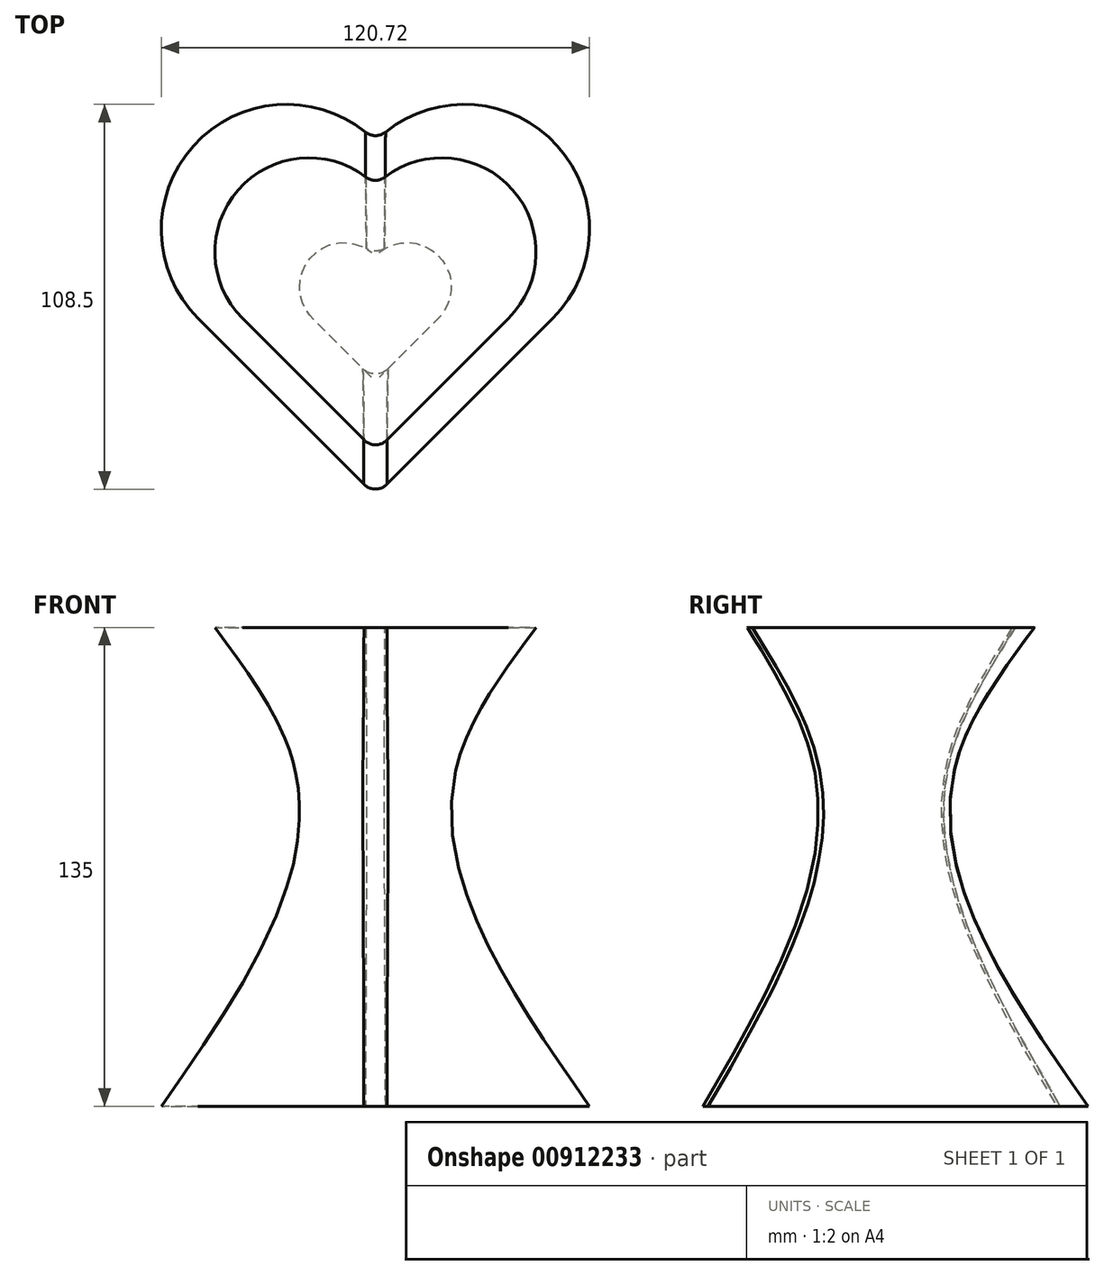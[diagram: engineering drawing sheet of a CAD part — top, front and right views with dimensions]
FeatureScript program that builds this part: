
annotation { "Feature Type Name" : "Feature", "Feature Type Description" : "" }
export const myFeature = defineFeature(function(context is Context, id is Id, definition is map)
    precondition{}
    {
        {
            var Q0;
            Q0=qCreatedBy(makeId("Top.planeOp"),FACE);
            var sketch = newSketch(context, id + "F0", { "sketchPlane" : qUnion([Q0])});
            skLineSegment(sketch, "E0.bottom", {"start": v(0, -50) * mm, "end": v(-50, 0) * mm});
            skLineSegment(sketch, "E0.top", {"start": v(50, 0) * mm, "end": v(0, 50) * mm, "construction": true});
            skLineSegment(sketch, "E0.left", {"start": v(0, -50) * mm, "end": v(50, 0) * mm});
            skLineSegment(sketch, "E0.right", {"start": v(-50, 0) * mm, "end": v(0, 50) * mm, "construction": true});
            skPoint(sketch, "E0.middle", {"position": v(0, 0) * mm});
            skArc(sketch, "E1", {"start": v(50, 0) * mm, "mid": v(50, 50) * mm, "end": v(0, 50) * mm});
            skArc(sketch, "E2", {"start": v(0, 50) * mm, "mid": v(-50, 50) * mm, "end": v(-50, 0) * mm});
            skLineSegment(sketch, "E3", {"start": v(0, -50) * mm, "end": v(0, 50) * mm, "construction": true});
            skLineSegment(sketch, "E4", {"start": v(50, 0) * mm, "end": v(-50, 0) * mm, "construction": true});
            skSolve(sketch);
        }
        {
            var Q0;
            Q0=qCreatedBy(makeId("Top.planeOp"),FACE);
            cPlane(context, id + "F1", {"entities" : qUnion([Q0]), "cplaneType" : CPlaneType.OFFSET, "offset" : 100 * mm, "width" : 150 * mm, "height" : 150 * mm});
        }
        {
            var Q0;
            Q0=qCreatedBy(id+"F1.planeOp",FACE);
            var sketch = newSketch(context, id + "F2", { "sketchPlane" : qUnion([Q0])});
            skLineSegment(sketch, "E5.bottom", {"start": v(0, -20) * mm, "end": v(-20, 0) * mm});
            skLineSegment(sketch, "E5.top", {"start": v(20, 0) * mm, "end": v(0, 20) * mm, "construction": true});
            skLineSegment(sketch, "E5.left", {"start": v(0, -20) * mm, "end": v(20, 0) * mm});
            skLineSegment(sketch, "E5.right", {"start": v(-20, 0) * mm, "end": v(0, 20) * mm, "construction": true});
            skPoint(sketch, "E5.middle", {"position": v(0, 0) * mm});
            skArc(sketch, "E6", {"start": v(20, 0) * mm, "mid": v(20, 20) * mm, "end": v(0, 20) * mm});
            skArc(sketch, "E7", {"start": v(0, 20) * mm, "mid": v(-20, 20) * mm, "end": v(-20, 0) * mm});
            skLineSegment(sketch, "E8", {"start": v(0, -20) * mm, "end": v(0, 20) * mm, "construction": true});
            skLineSegment(sketch, "E9", {"start": v(20, 0) * mm, "end": v(-20, 0) * mm, "construction": true});
            skSolve(sketch);
        }
        {
            var Q0;
            Q0=qCreatedBy(id+"F1.planeOp",FACE);
            cPlane(context, id + "F3", {"entities" : qUnion([Q0]), "cplaneType" : CPlaneType.OFFSET, "offset" : 35 * mm, "width" : 150 * mm, "height" : 150 * mm});
        }
        {
            var Q0;
            Q0=qCreatedBy(id+"F3.planeOp",FACE);
            var sketch = newSketch(context, id + "F4", { "sketchPlane" : qUnion([Q0])});
            skLineSegment(sketch, "E10.bottom", {"start": v(0, -37.5) * mm, "end": v(-37.5, 0.01) * mm});
            skLineSegment(sketch, "E10.top", {"start": v(37.5, -0.01) * mm, "end": v(0, 37.5) * mm, "construction": true});
            skLineSegment(sketch, "E10.left", {"start": v(0, -37.5) * mm, "end": v(37.5, -0.01) * mm});
            skLineSegment(sketch, "E10.right", {"start": v(-37.5, 0.01) * mm, "end": v(0, 37.5) * mm, "construction": true});
            skPoint(sketch, "E10.middle", {"position": v(0, 0) * mm});
            skArc(sketch, "E11", {"start": v(37.5, -0.01) * mm, "mid": v(37.5, 37.5) * mm, "end": v(0, 37.5) * mm});
            skArc(sketch, "E12", {"start": v(0, 37.5) * mm, "mid": v(-37.5, 37.5) * mm, "end": v(-37.5, 0.01) * mm});
            skLineSegment(sketch, "E13", {"start": v(0, -37.5) * mm, "end": v(0, 37.5) * mm, "construction": true});
            skLineSegment(sketch, "E14", {"start": v(37.5, -0.01) * mm, "end": v(-37.5, 0.01) * mm, "construction": true});
            skSolve(sketch);
        }
        {
            var Q0;
            Q0=makeQuery(id+"F0.imprint","IMPRINT",FACE,{"disambiguationData":[TD([[makeQuery(id+"F0.imprint","IMPRINT",EDGE,{"derivedFrom":sQuery(id+"F0.wireOp",EDGE,"E0.bottom")}),-1.0]])]});
            var Q1;
            Q1=makeQuery(id+"F2.imprint","IMPRINT",FACE,{"disambiguationData":[TD([[makeQuery(id+"F2.imprint","IMPRINT",EDGE,{"derivedFrom":sQuery(id+"F2.wireOp",EDGE,"E5.bottom")}),-1.0]])]});
            var Q2;
            Q2=makeQuery(id+"F4.imprint","IMPRINT",FACE,{"disambiguationData":[TD([[makeQuery(id+"F4.imprint","IMPRINT",EDGE,{"derivedFrom":sQuery(id+"F4.wireOp",EDGE,"E10.bottom")}),-1.0]])]});
            var Q3;
            Q3=makeQuery(id+"F0.imprint","IMPRINT",FACE,{"disambiguationData":[TD([[makeQuery(id+"F0.imprint","IMPRINT",EDGE,{"derivedFrom":sQuery(id+"F0.wireOp",EDGE,"E0.bottom")}),-1.0]])]});
            var Q4;
            Q4=makeQuery(id+"F2.imprint","IMPRINT",FACE,{"disambiguationData":[TD([[makeQuery(id+"F2.imprint","IMPRINT",EDGE,{"derivedFrom":sQuery(id+"F2.wireOp",EDGE,"E5.bottom")}),-1.0]])]});
            var Q5;
            Q5=makeQuery(id+"F4.imprint","IMPRINT",FACE,{"disambiguationData":[TD([[makeQuery(id+"F4.imprint","IMPRINT",EDGE,{"derivedFrom":sQuery(id+"F4.wireOp",EDGE,"E10.bottom")}),-1.0]])]});
            loft(context, id + "F5", {"sheetProfilesArray" : [{ "sheetProfileEntities" : qUnion([Q0]) }, { "sheetProfileEntities" : qUnion([Q1]) }, { "sheetProfileEntities" : qUnion([Q2]) }], "wireProfilesArray" : [{ "wireProfileEntities" : qUnion([Q3]) }, { "wireProfileEntities" : qUnion([Q4]) }, { "wireProfileEntities" : qUnion([Q5]) }]});
        }
        {
            var Q0;
            Q0=makeQuery(id+"F5.opLoft","SWEPT_EDGE",EDGE,{"disambiguationData":[OSD([sQuery(id+"F0.wireOp",EDGE,"E0.bottom"),sQuery(id+"F0.wireOp",EDGE,"E0.left"),sQuery(id+"F2.wireOp",EDGE,"E5.bottom"),sQuery(id+"F2.wireOp",EDGE,"E5.left"),sQuery(id+"F4.wireOp",EDGE,"E10.bottom"),sQuery(id+"F4.wireOp",EDGE,"E10.left")])]});
            var Q1;
            Q1=makeQuery(id+"F5.opLoft","SWEPT_EDGE",EDGE,{"disambiguationData":[OSD([sQuery(id+"F0.wireOp",EDGE,"E1"),sQuery(id+"F0.wireOp",EDGE,"E2"),sQuery(id+"F2.wireOp",EDGE,"E6"),sQuery(id+"F2.wireOp",EDGE,"E7"),sQuery(id+"F4.wireOp",EDGE,"E11"),sQuery(id+"F4.wireOp",EDGE,"E12")])]});
            fillet(context, id + "F6", {"entities" : qUnion([Q0, Q1]), "radius" : 5 * mm, "tangentPropagation" : true, "allowEdgeOverflow" : false});
        }
    });
